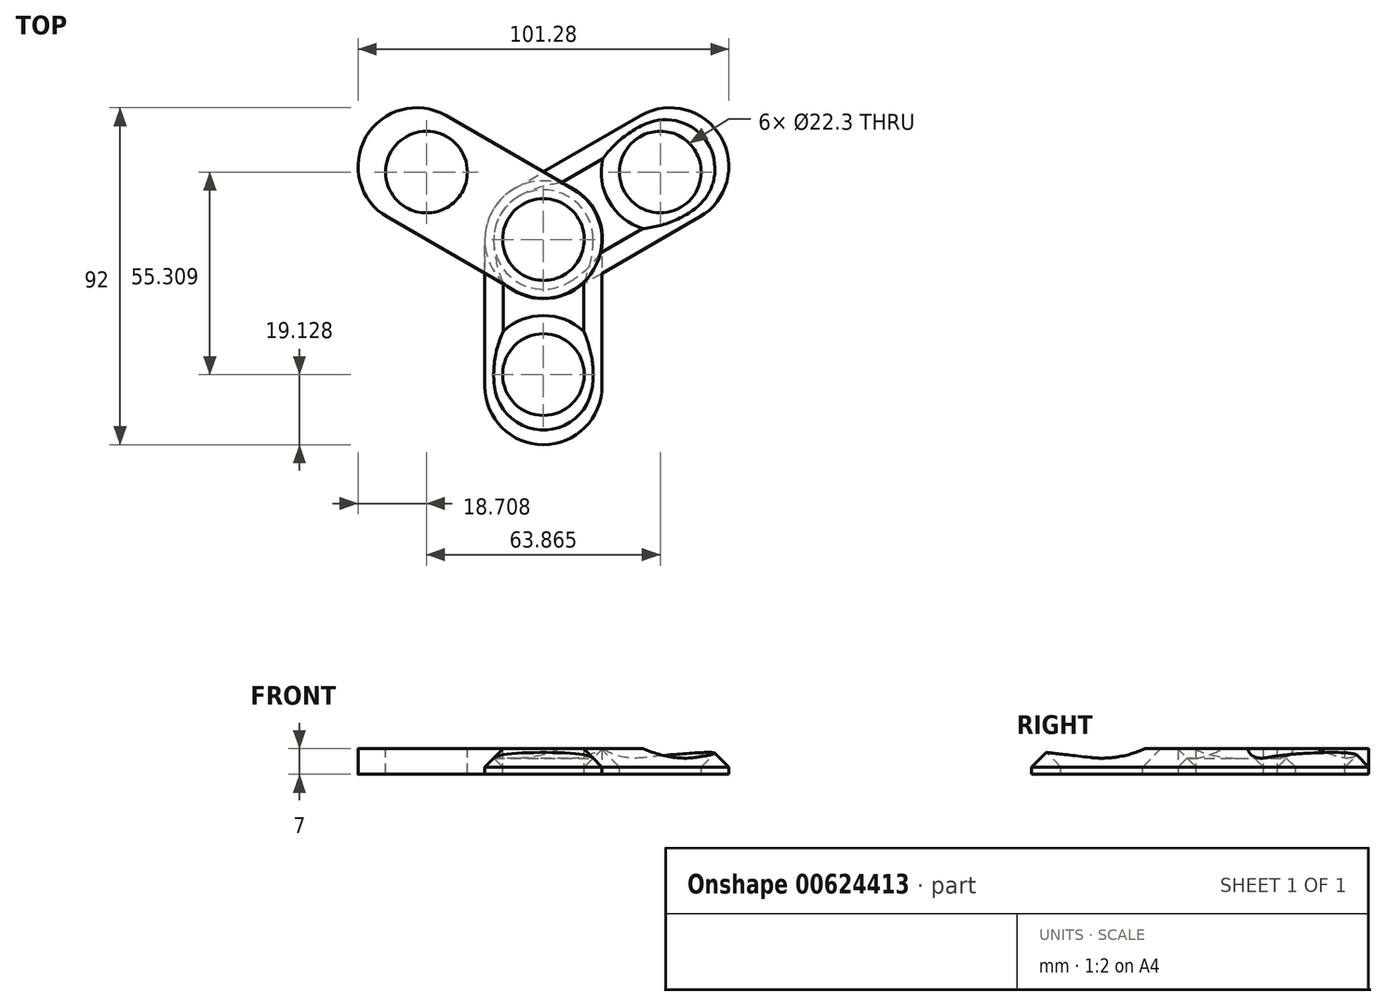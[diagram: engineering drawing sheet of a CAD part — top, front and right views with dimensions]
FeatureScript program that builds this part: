
annotation { "Feature Type Name" : "Feature", "Feature Type Description" : "" }
export const myFeature = defineFeature(function(context is Context, id is Id, definition is map)
    precondition{}
    {
        {
            var Q0;
            Q0=qCreatedBy(makeId("Top.planeOp"),FACE);
            var sketch = newSketch(context, id + "F0", { "sketchPlane" : qUnion([Q0])});
            skCircle(sketch, "E0", {"center": v(0, 0) * mm, "radius": 16 * mm});
            skCircle(sketch, "E1", {"center": v(0, -40) * mm, "radius": 16 * mm});
            skLineSegment(sketch, "E2", {"start": v(-16, 0) * mm, "end": v(-16, -40) * mm});
            skLineSegment(sketch, "E3", {"start": v(16, 0) * mm, "end": v(16, -40) * mm});
            skSolve(sketch);
        }
        {
            var Q0;
            Q0 = qSketchRegion(id + "F0", true);
            extrude(context, id + "F1", {"entities" : qUnion([Q0]), "depth" : 7 * mm, "offsetDistance" : 25 * mm});
        }
        {
            var Q0;
            Q0=makeQuery(id+"F1.opExtrude","CAP_FACE",FACE,{"disambiguationData":[OSD([sQuery(id+"F0.wireOp",EDGE,"E0"),sQuery(id+"F0.wireOp",EDGE,"E1"),sQuery(id+"F0.wireOp",EDGE,"E2"),sQuery(id+"F0.wireOp",EDGE,"E3")])],"isStart":false});
            var sketch = newSketch(context, id + "F2", { "sketchPlane" : qUnion([Q0])});
            skCircle(sketch, "E4", {"center": v(0, 0) * mm, "radius": 11.15 * mm});
            skCircle(sketch, "E5", {"center": v(0, -36.87) * mm, "radius": 11.15 * mm});
            skSolve(sketch);
        }
        {
            var Q0;
            Q0 = qSketchRegion(id + "F2", true);
            extrude(context, id + "F3", {"entities" : qUnion([Q0]), "operationType" : NewBodyOperationType.REMOVE, "endBound" : BoundingType.THROUGH_ALL, "oppositeDirection" : true, "depth" : 25 * mm, "offsetDistance" : 25 * mm});
        }
        {
            var Q0;
            Q0=qCreatedBy(makeId("Front.planeOp"),FACE);
            var sketch = newSketch(context, id + "F4", { "sketchPlane" : qUnion([Q0])});
            skLineSegment(sketch, "E6", {"start": v(0, 0) * mm, "end": v(0, -20.09) * mm});
            skSolve(sketch);
        }
        {
            var Q0;
            Q0=makeQuery(id+"F1.opExtrude","SWEPT_BODY",BODY,{"disambiguationData":[OSD([sQuery(id+"F0.wireOp",EDGE,"E0"),sQuery(id+"F0.wireOp",EDGE,"E1"),sQuery(id+"F0.wireOp",EDGE,"E2"),sQuery(id+"F0.wireOp",EDGE,"E3")])]});
            var Q1;
            Q1=sQuery(id+"F4.wireOp",EDGE,"E6");
            circularPattern(context, id + "F5", {"entities" : qUnion([Q0]), "axis" : qUnion([Q1]), "angle" : 360 * degree, "instanceCount" : 3, "equalSpace" : true});
        }
        {
            var Q0;
            Q0=makeQuery(id+"F5.opPattern","COPY",EDGE,{"derivedFrom":makeQuery(id+"F1.opExtrude","SWEPT_EDGE",EDGE,{"disambiguationData":[OSD([sQuery(id+"F0.wireOp",EDGE,"E1"),sQuery(id+"F0.wireOp",EDGE,"E2")])]}),"instanceName":"1"});
            var Q1;
            Q1=makeQuery(id+"F5.opPattern","COPY",FACE,{"derivedFrom":makeQuery(id+"F1.opExtrude","CAP_FACE",FACE,{"disambiguationData":[OSD([sQuery(id+"F0.wireOp",EDGE,"E0"),sQuery(id+"F0.wireOp",EDGE,"E1"),sQuery(id+"F0.wireOp",EDGE,"E2"),sQuery(id+"F0.wireOp",EDGE,"E3")])],"isStart":false}),"instanceName":"1"});
            var Q2;
            Q2=makeQuery(id+"F5.opPattern","COPY",EDGE,{"derivedFrom":makeQuery(id+"F1.opExtrude","SWEPT_EDGE",EDGE,{"disambiguationData":[OSD([sQuery(id+"F0.wireOp",EDGE,"E1"),sQuery(id+"F0.wireOp",EDGE,"E3")])]}),"instanceName":"1"});
            var Q3;
            Q3=makeQuery(id+"F5.opPattern","COPY",FACE,{"derivedFrom":makeQuery(id+"F1.opExtrude","SWEPT_FACE",FACE,{"disambiguationData":[OSD([sQuery(id+"F0.wireOp",EDGE,"E3")])]}),"instanceName":"1"});
            var Q4;
            Q4=makeQuery(id+"F5.opPattern","COPY",EDGE,{"derivedFrom":makeQuery(id+"F1.opExtrude","CAP_EDGE",EDGE,{"disambiguationData":[OSD([sQuery(id+"F0.wireOp",EDGE,"E2")])],"isStart":true}),"instanceName":"1"});
            fillet(context, id + "F6", {"entities" : qUnion([Q0, Q1, Q2, Q3, Q4]), "tangentPropagation" : true, "radius" : 0.02 * mm, "defaultsChanged" : false, "vertexSettings" : [], "allowEdgeOverflow" : false});
        }
        {
            var Q0;
            Q0=makeQuery(id+"F5.opPattern","COPY",FACE,{"derivedFrom":makeQuery(id+"F1.opExtrude","CAP_FACE",FACE,{"disambiguationData":[OSD([sQuery(id+"F0.wireOp",EDGE,"E0"),sQuery(id+"F0.wireOp",EDGE,"E1"),sQuery(id+"F0.wireOp",EDGE,"E2"),sQuery(id+"F0.wireOp",EDGE,"E3")])],"isStart":false}),"instanceName":"2"});
            chamfer(context, id + "F7", {"entities" : qUnion([Q0]), "width" : 5 * mm, "tangentPropagation" : true});
        }
        {
            var Q0;
            Q0=makeQuery(id+"F1.opExtrude","CAP_FACE",FACE,{"disambiguationData":[OSD([sQuery(id+"F0.wireOp",EDGE,"E0"),sQuery(id+"F0.wireOp",EDGE,"E1"),sQuery(id+"F0.wireOp",EDGE,"E2"),sQuery(id+"F0.wireOp",EDGE,"E3")])],"isStart":false});
            chamfer(context, id + "F8", {"entities" : qUnion([Q0]), "width" : 5 * mm, "tangentPropagation" : true});
        }
    });
